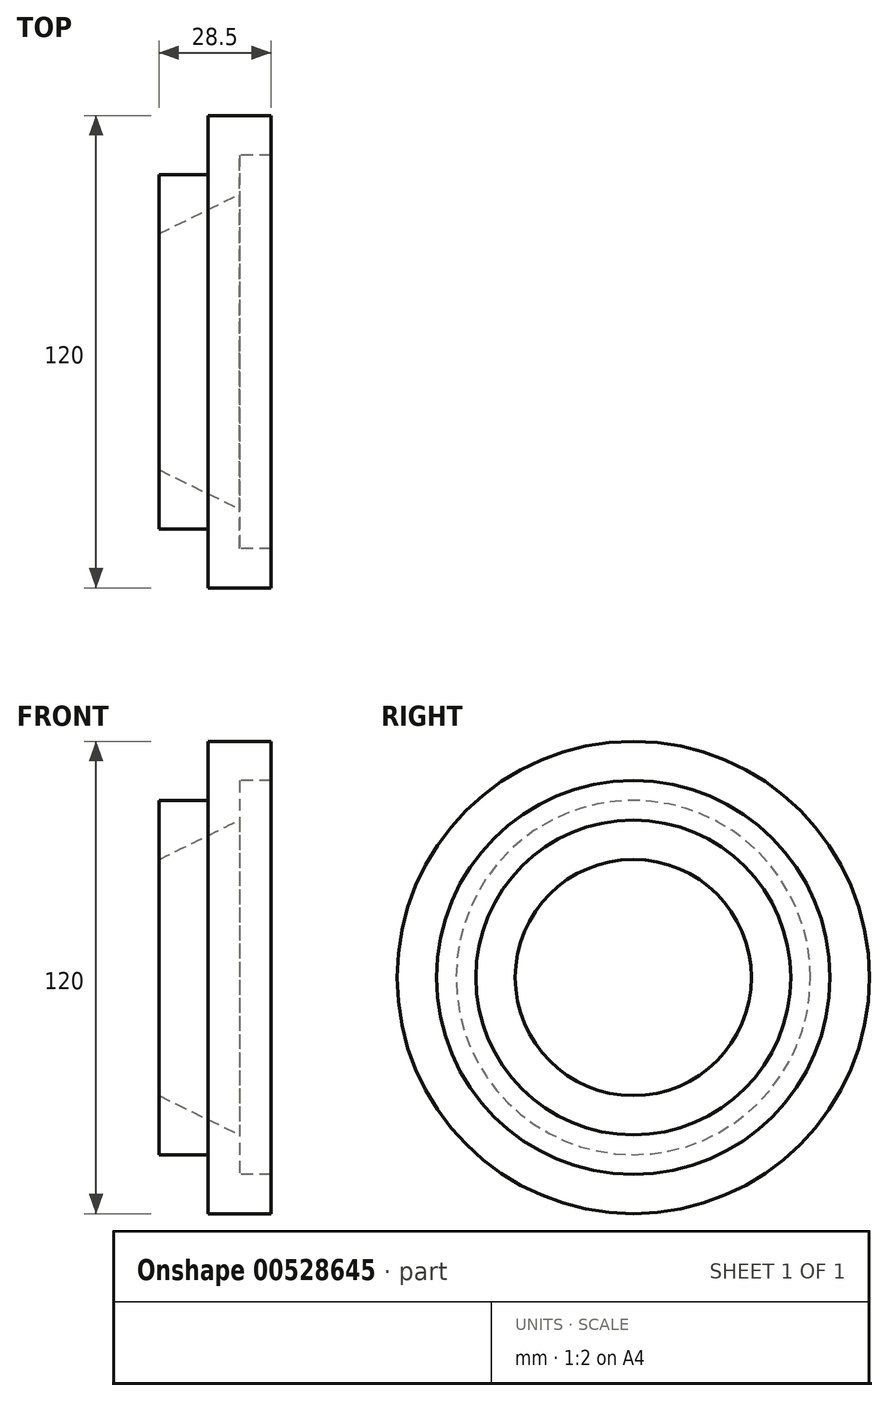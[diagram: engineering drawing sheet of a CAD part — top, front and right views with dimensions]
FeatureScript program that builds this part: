
annotation { "Feature Type Name" : "Feature", "Feature Type Description" : "" }
export const myFeature = defineFeature(function(context is Context, id is Id, definition is map)
    precondition{}
    {
        {
            var Q0;
            Q0=qCreatedBy(makeId("Front.planeOp"),FACE);
            var sketch = newSketch(context, id + "F0", { "sketchPlane" : qUnion([Q0])});
            skLineSegment(sketch, "E0", {"start": v(0, 60) * mm, "end": v(0, 0) * mm});
            skLineSegment(sketch, "E1", {"start": v(0, 60) * mm, "end": v(-16, 60) * mm});
            skLineSegment(sketch, "E2", {"start": v(-16, 60) * mm, "end": v(-16, 45) * mm});
            skLineSegment(sketch, "E3", {"start": v(-16, 45) * mm, "end": v(-28.5, 45) * mm});
            skLineSegment(sketch, "E4", {"start": v(0, 50) * mm, "end": v(-8, 50) * mm});
            skLineSegment(sketch, "E5", {"start": v(-28.5, 45) * mm, "end": v(-28.5, 30) * mm});
            skLineSegment(sketch, "E6", {"start": v(-28.5, 30) * mm, "end": v(-28.5, 0) * mm});
            skLineSegment(sketch, "E7", {"start": v(-28.5, 0) * mm, "end": v(0, 0) * mm});
            skLineSegment(sketch, "E8", {"start": v(-8, 50) * mm, "end": v(-8, 40) * mm});
            skLineSegment(sketch, "E9", {"start": v(-28.5, 30) * mm, "end": v(-8, 40) * mm});
            skSolve(sketch);
        }
        {
            var Q0;
            {var subQ1=sQuery(id+"F0.wireOp",EDGE,"E1");Q0=makeQuery(id+"F0.imprint","IMPRINT",FACE,{"disambiguationData":[TD([[makeQuery(id+"F0.imprint","IMPRINT",EDGE,{"derivedFrom":subQ1}),1.0]])]});}
            var Q1;
            Q1=sQuery(id+"F0.wireOp",EDGE,"E7");
            revolve(context, id + "F1", {"entities" : qUnion([Q0]), "axis" : qUnion([Q1]), "revolveType" : RevolveType.FULL});
        }
    });
